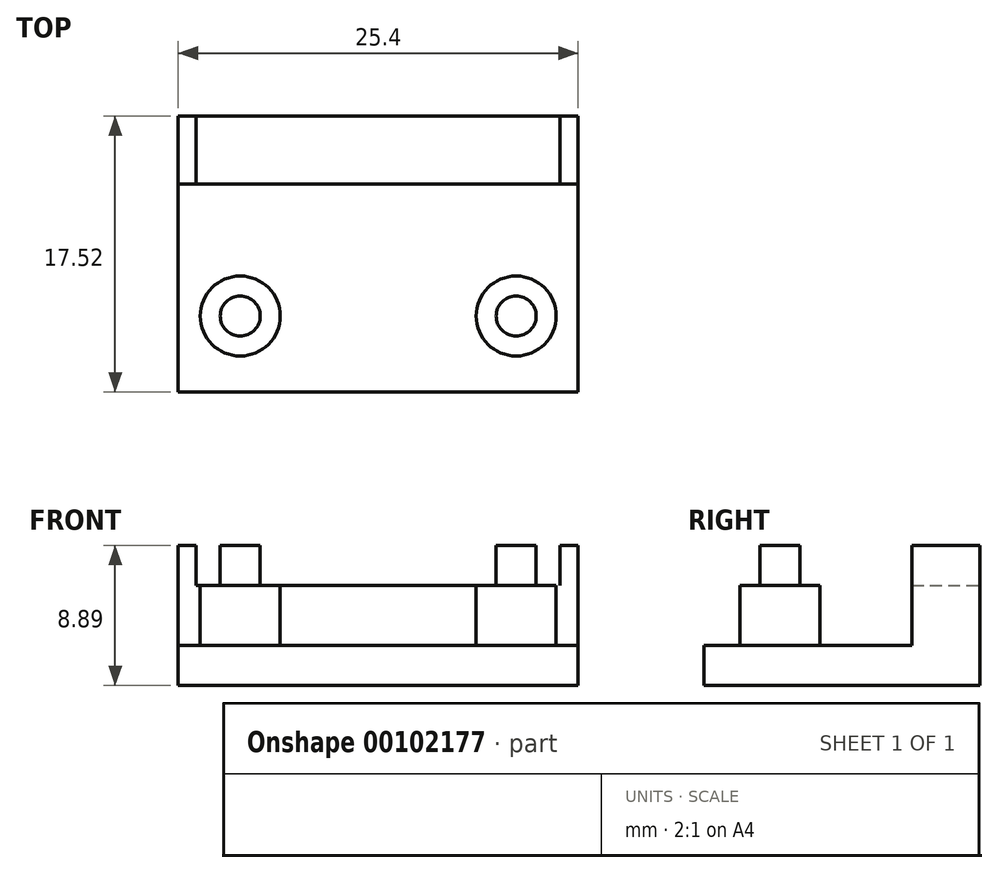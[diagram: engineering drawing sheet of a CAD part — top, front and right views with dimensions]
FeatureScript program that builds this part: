
annotation { "Feature Type Name" : "Feature", "Feature Type Description" : "" }
export const myFeature = defineFeature(function(context is Context, id is Id, definition is map)
    precondition{}
    {
        {
            var Q0;
            Q0=qCreatedBy(makeId("Top.planeOp"),FACE);
            var sketch = newSketch(context, id + "F0", { "sketchPlane" : qUnion([Q0])});
            skLineSegment(sketch, "E0.bottom", {"start": v(-12.7, 8.76) * mm, "end": v(12.7, 8.76) * mm});
            skLineSegment(sketch, "E0.top", {"start": v(-12.7, -8.76) * mm, "end": v(12.7, -8.76) * mm});
            skLineSegment(sketch, "E0.left", {"start": v(-12.7, 8.76) * mm, "end": v(-12.7, -8.76) * mm});
            skLineSegment(sketch, "E0.right", {"start": v(12.7, 8.76) * mm, "end": v(12.7, -8.76) * mm});
            skPoint(sketch, "E1", {"position": v(0, 8.76) * mm});
            skPoint(sketch, "E2", {"position": v(12.7, 0) * mm});
            skSolve(sketch);
        }
        {
            var Q0;
            Q0 = qSketchRegion(id + "F0", true);
            extrude(context, id + "F1", {"entities" : qUnion([Q0]), "depth" : 2.54 * mm});
        }
        {
            var Q0;
            Q0=makeQuery(id+"F1.opExtrude","CAP_FACE",FACE,{"disambiguationData":[OSD([sQuery(id+"F0.wireOp",EDGE,"E0.bottom"),sQuery(id+"F0.wireOp",EDGE,"E0.top"),sQuery(id+"F0.wireOp",EDGE,"E0.left"),sQuery(id+"F0.wireOp",EDGE,"E0.right")])],"isStart":false});
            var sketch = newSketch(context, id + "F2", { "sketchPlane" : qUnion([Q0])});
            skLineSegment(sketch, "E3.bottom", {"start": v(-12.7, 8.76) * mm, "end": v(12.7, 8.76) * mm});
            skLineSegment(sketch, "E3.top", {"start": v(-12.7, 4.44) * mm, "end": v(12.7, 4.44) * mm});
            skLineSegment(sketch, "E3.left", {"start": v(-12.7, 8.76) * mm, "end": v(-12.7, 4.44) * mm});
            skLineSegment(sketch, "E3.right", {"start": v(12.7, 8.76) * mm, "end": v(12.7, 4.44) * mm});
            skCircle(sketch, "E4", {"center": v(-8.76, -3.94) * mm, "radius": 2.54 * mm});
            skCircle(sketch, "E5", {"center": v(8.76, -3.94) * mm, "radius": 2.54 * mm});
            skLineSegment(sketch, "E6", {"start": v(-8.76, -3.94) * mm, "end": v(8.76, -3.94) * mm, "construction": true});
            skPoint(sketch, "E7", {"position": v(0, -3.94) * mm});
            skSolve(sketch);
        }
        {
            var Q0;
            Q0 = qSketchRegion(id + "F2", true);
            extrude(context, id + "F3", {"entities" : qUnion([Q0]), "operationType" : NewBodyOperationType.ADD, "depth" : 3.8 * mm});
        }
        {
            var Q0;
            Q0=makeQuery(id+"F3.opExtrude","CAP_FACE",FACE,{"disambiguationData":[OSD([sQuery(id+"F2.wireOp",EDGE,"E4")])],"isStart":false});
            var sketch = newSketch(context, id + "F4", { "sketchPlane" : qUnion([Q0])});
            skLineSegment(sketch, "E8.bottom", {"start": v(-12.7, 8.76) * mm, "end": v(-11.56, 8.76) * mm});
            skLineSegment(sketch, "E8.top", {"start": v(-12.7, 4.44) * mm, "end": v(-11.56, 4.44) * mm});
            skLineSegment(sketch, "E8.left", {"start": v(-12.7, 8.76) * mm, "end": v(-12.7, 4.44) * mm});
            skLineSegment(sketch, "E8.right", {"start": v(-11.56, 8.76) * mm, "end": v(-11.56, 4.44) * mm});
            skLineSegment(sketch, "E9.bottom", {"start": v(12.7, 4.44) * mm, "end": v(11.56, 4.44) * mm});
            skLineSegment(sketch, "E9.top", {"start": v(12.7, 8.76) * mm, "end": v(11.56, 8.76) * mm});
            skLineSegment(sketch, "E9.left", {"start": v(12.7, 4.44) * mm, "end": v(12.7, 8.76) * mm});
            skLineSegment(sketch, "E9.right", {"start": v(11.56, 4.44) * mm, "end": v(11.56, 8.76) * mm});
            skCircle(sketch, "E10", {"center": v(-8.76, -3.94) * mm, "radius": 1.27 * mm});
            skCircle(sketch, "E11", {"center": v(8.76, -3.94) * mm, "radius": 1.27 * mm});
            skSolve(sketch);
        }
        {
            var Q0;
            Q0 = qSketchRegion(id + "F4", true);
            extrude(context, id + "F5", {"entities" : qUnion([Q0]), "operationType" : NewBodyOperationType.ADD, "depth" : 2.54 * mm});
        }
    });
